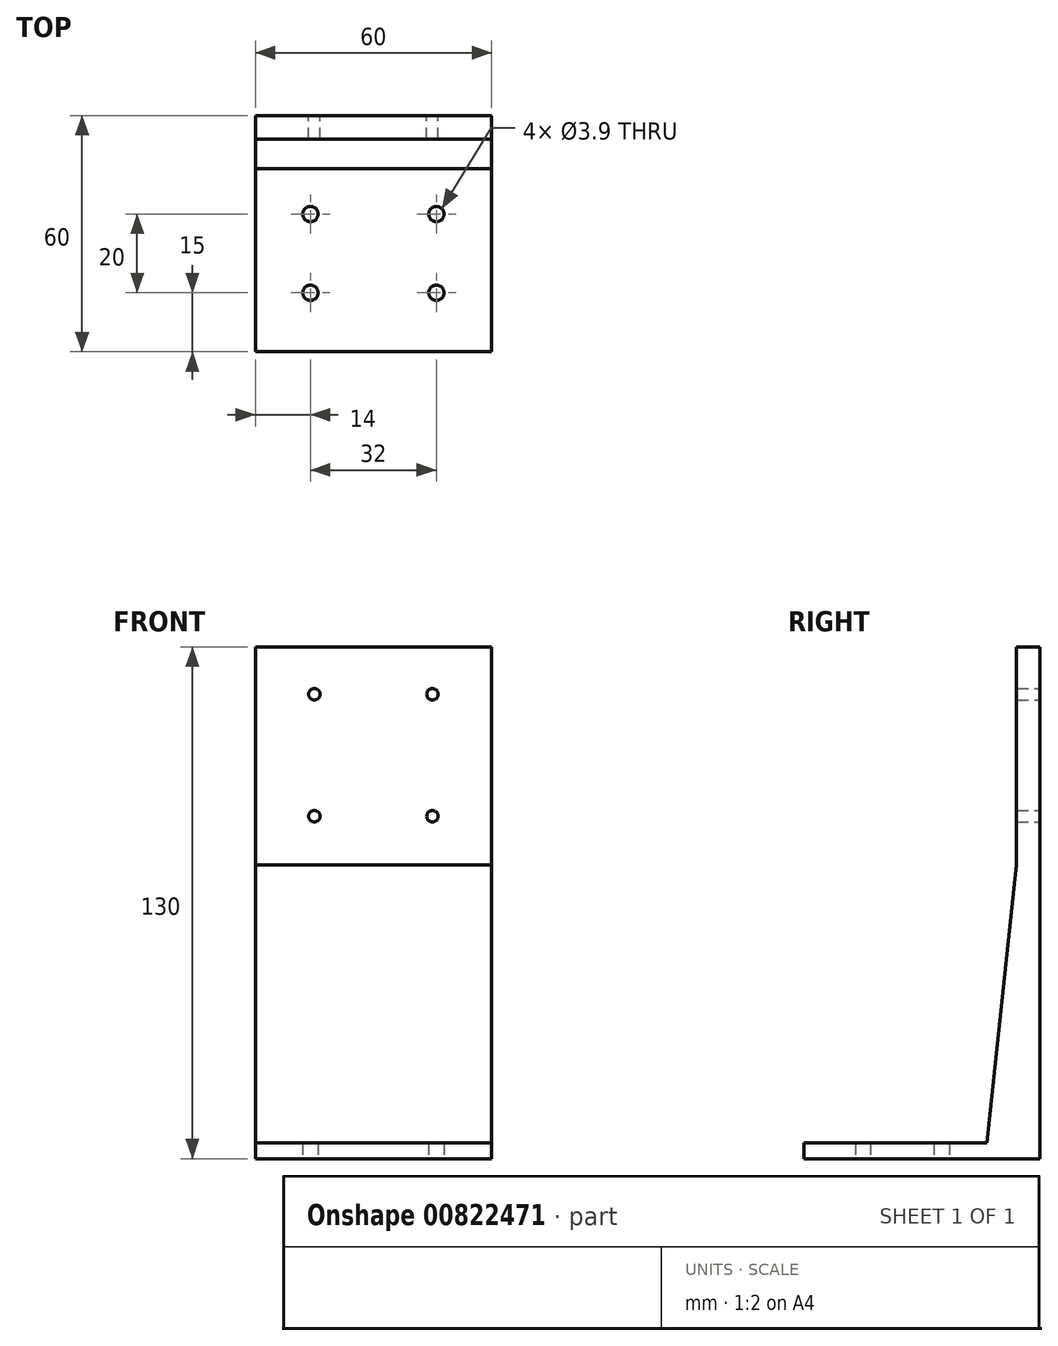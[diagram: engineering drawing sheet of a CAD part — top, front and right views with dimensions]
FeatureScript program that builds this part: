
annotation { "Feature Type Name" : "Feature", "Feature Type Description" : "" }
export const myFeature = defineFeature(function(context is Context, id is Id, definition is map)
    precondition{}
    {
        {
            var Q0;
            Q0=qCreatedBy(makeId("Top.planeOp"),FACE);
            var sketch = newSketch(context, id + "F0", { "sketchPlane" : qUnion([Q0])});
            skLineSegment(sketch, "E0.bottom", {"start": v(-30, 30) * mm, "end": v(30, 30) * mm});
            skLineSegment(sketch, "E0.top", {"start": v(-30, -30) * mm, "end": v(30, -30) * mm});
            skLineSegment(sketch, "E0.left", {"start": v(-30, 30) * mm, "end": v(-30, -30) * mm});
            skLineSegment(sketch, "E0.right", {"start": v(30, 30) * mm, "end": v(30, -30) * mm});
            skPoint(sketch, "E0.middle", {"position": v(0, 0) * mm});
            skCircle(sketch, "E1", {"center": v(-16, -15) * mm, "radius": 1.95 * mm});
            skCircle(sketch, "E2", {"center": v(16, -15) * mm, "radius": 1.95 * mm});
            skCircle(sketch, "E3", {"center": v(-16, 5) * mm, "radius": 1.95 * mm});
            skCircle(sketch, "E4", {"center": v(16, 5) * mm, "radius": 1.95 * mm});
            skSolve(sketch);
        }
        {
            var Q0;
            Q0=makeQuery(id+"F0.imprint","IMPRINT",FACE,{"disambiguationData":[TD([[makeQuery(id+"F0.imprint","IMPRINT",EDGE,{"derivedFrom":sQuery(id+"F0.wireOp",EDGE,"E0.bottom")}),-1.0]])]});
            extrude(context, id + "F1", {"entities" : qUnion([Q0]), "depth" : 4 * mm, "offsetDistance" : 25 * mm});
        }
        {
            var Q0;
            Q0=makeQuery(id+"F1.opExtrude","SWEPT_FACE",FACE,{"disambiguationData":[OSD([sQuery(id+"F0.wireOp",EDGE,"E0.bottom")])]});
            var sketch = newSketch(context, id + "F2", { "sketchPlane" : qUnion([Q0])});
            skLineSegment(sketch, "E5.bottom", {"start": v(-30, 0) * mm, "end": v(30, 0) * mm});
            skLineSegment(sketch, "E5.top", {"start": v(-30, 130) * mm, "end": v(30, 130) * mm});
            skLineSegment(sketch, "E5.left", {"start": v(-30, 0) * mm, "end": v(-30, 130) * mm});
            skLineSegment(sketch, "E5.right", {"start": v(30, 0) * mm, "end": v(30, 130) * mm});
            skCircle(sketch, "E6", {"center": v(-15, 118) * mm, "radius": 1.45 * mm});
            skCircle(sketch, "E7", {"center": v(15, 118) * mm, "radius": 1.45 * mm});
            skCircle(sketch, "E8", {"center": v(-15, 87) * mm, "radius": 1.45 * mm});
            skCircle(sketch, "E9", {"center": v(15, 87) * mm, "radius": 1.45 * mm});
            skSolve(sketch);
        }
        {
            var Q0;
            {var subQ2=sQuery(id+"F2.wireOp",EDGE,"E5.top");Q0=makeQuery(id+"F2.imprint","IMPRINT",FACE,{"disambiguationData":[TD([[makeQuery(id+"F2.imprint","IMPRINT",EDGE,{"derivedFrom":subQ2}),-1.0]])]});}
            extrude(context, id + "F3", {"entities" : qUnion([Q0]), "operationType" : NewBodyOperationType.ADD, "oppositeDirection" : true, "depth" : 6 * mm, "offsetDistance" : 25 * mm});
        }
        {
            var Q0;
            Q0=makeQuery(id+"F3.boolean.opBoolean","MERGE",FACE,{"derivedFrom":[makeQuery(id+"F1.opExtrude","SWEPT_FACE",FACE,{"disambiguationData":[OSD([sQuery(id+"F0.wireOp",EDGE,"E0.right")])]}),makeQuery(id+"F3.opExtrude","SWEPT_FACE",FACE,{"disambiguationData":[OSD([sQuery(id+"F2.wireOp",EDGE,"E5.left")])]})]});
            var sketch = newSketch(context, id + "F4", { "sketchPlane" : qUnion([Q0])});
            skLineSegment(sketch, "E10", {"start": v(16.5, 4) * mm, "end": v(24, 74.6) * mm});
            skPoint(sketch, "E11", {"position": v(24, 67) * mm});
            skSolve(sketch);
        }
        {
            var Q0;
            {var subQ0=sQuery(id+"F4.wireOp",EDGE,"E10");Q0=makeQuery(id+"F4.imprint","IMPRINT",FACE,{"disambiguationData":[TD([[makeQuery(id+"F4.imprint","IMPRINT",EDGE,{"derivedFrom":subQ0}),-1.0]])]});}
            extrude(context, id + "F5", {"entities" : qUnion([Q0]), "operationType" : NewBodyOperationType.ADD, "oppositeDirection" : true, "depth" : 60 * mm, "offsetDistance" : 25 * mm});
        }
    });
